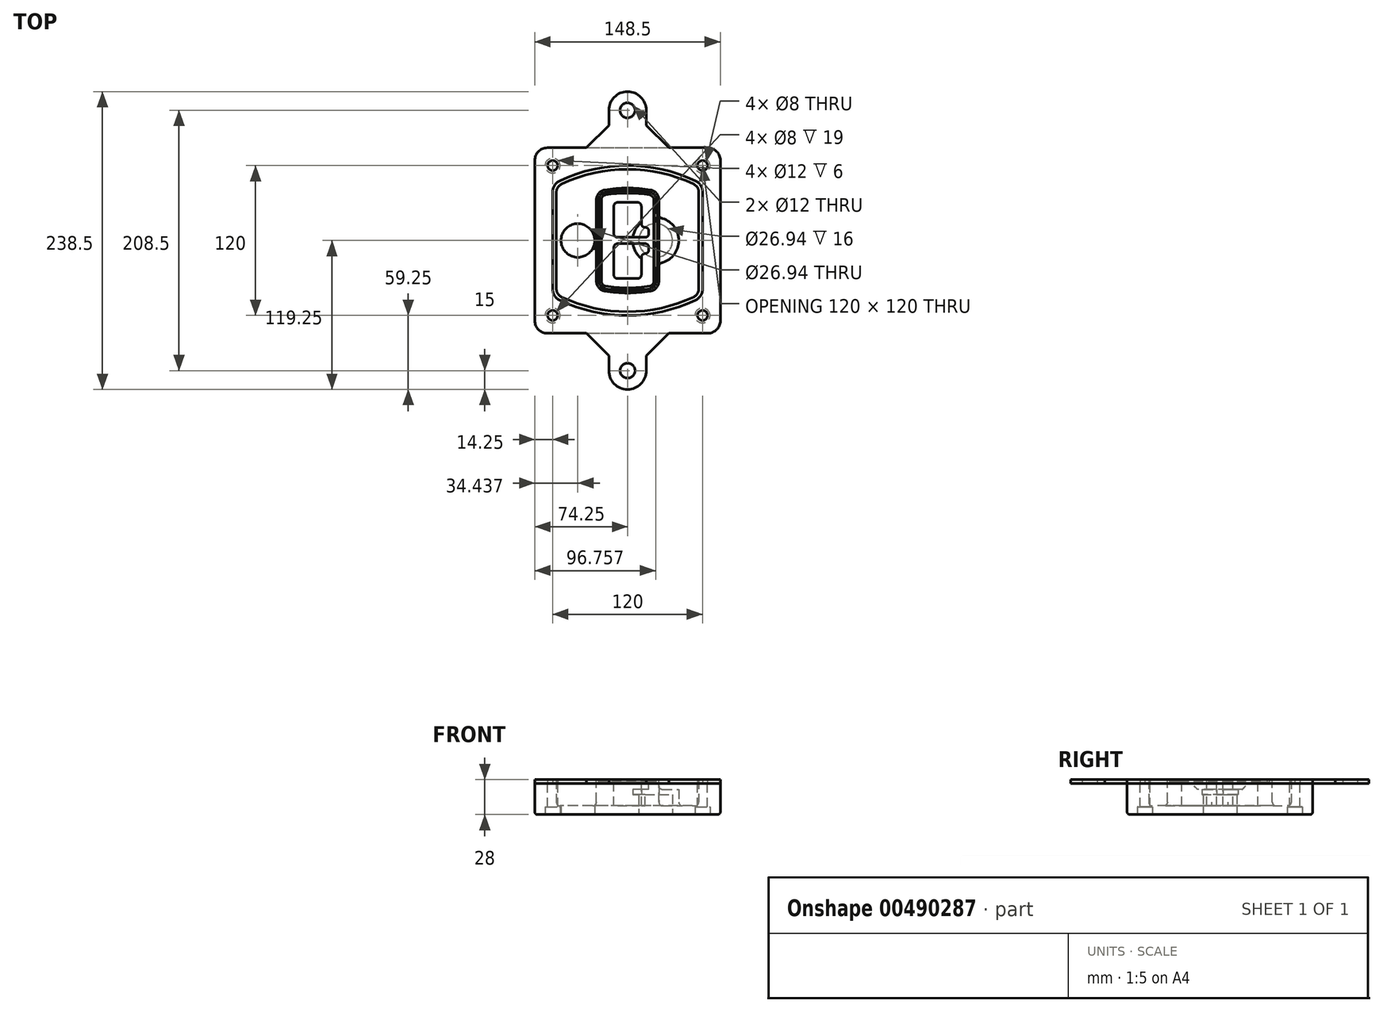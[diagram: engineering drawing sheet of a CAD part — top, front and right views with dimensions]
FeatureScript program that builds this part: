
annotation { "Feature Type Name" : "Feature", "Feature Type Description" : "" }
export const myFeature = defineFeature(function(context is Context, id is Id, definition is map)
    precondition{}
    {
        {
            var Q0;
            Q0=qCreatedBy(makeId("Top.planeOp"),FACE);
            var sketch = newSketch(context, id + "F0", { "sketchPlane" : qUnion([Q0])});
            skPoint(sketch, "E0.rect.middle", {"position": v(0, 0) * mm});
            skLineSegment(sketch, "E1.bottom", {"start": v(-64.25, -74.25) * mm, "end": v(64.25, -74.25) * mm});
            skLineSegment(sketch, "E1.top", {"start": v(-64.25, 74.25) * mm, "end": v(64.25, 74.25) * mm});
            skLineSegment(sketch, "E1.left", {"start": v(-74.25, -64.25) * mm, "end": v(-74.25, 64.25) * mm});
            skLineSegment(sketch, "E1.right", {"start": v(74.25, -64.25) * mm, "end": v(74.25, 64.25) * mm});
            skLineSegment(sketch, "E2", {"start": v(-74.25, 74.25) * mm, "end": v(74.25, -74.25) * mm, "construction": true});
            skLineSegment(sketch, "E3", {"start": v(74.25, 74.25) * mm, "end": v(-74.25, -74.25) * mm, "construction": true});
            skCircle(sketch, "E4", {"center": v(-60, 60) * mm, "radius": 4 * mm});
            skCircle(sketch, "E5", {"center": v(60, 60) * mm, "radius": 4 * mm});
            skCircle(sketch, "E6", {"center": v(60, -60) * mm, "radius": 4 * mm});
            skCircle(sketch, "E7", {"center": v(-60, -60) * mm, "radius": 4 * mm});
            skLineSegment(sketch, "E8", {"start": v(-60, 60) * mm, "end": v(60, 60) * mm, "construction": true});
            skLineSegment(sketch, "E9", {"start": v(60, 60) * mm, "end": v(60, -60) * mm, "construction": true});
            skLineSegment(sketch, "E10", {"start": v(60, -60) * mm, "end": v(-60, -60) * mm, "construction": true});
            skLineSegment(sketch, "E11", {"start": v(-60, -60) * mm, "end": v(-60, 60) * mm, "construction": true});
            skLineSegment(sketch, "E12", {"start": v(-60, 38.83) * mm, "end": v(-60, -38.83) * mm});
            skLineSegment(sketch, "E13", {"start": v(60, 38.83) * mm, "end": v(60, -38.83) * mm});
            skArc(sketch, "E14", {"start": v(54.26, 47.88) * mm, "mid": v(0, 60) * mm, "end": v(-54.26, 47.88) * mm});
            skArc(sketch, "E15", {"start": v(-54.26, -47.88) * mm, "mid": v(0, -60) * mm, "end": v(54.26, -47.88) * mm});
            skLineSegment(sketch, "E16", {"start": v(-60, 0) * mm, "end": v(60, 0) * mm, "construction": true});
            skPoint(sketch, "E17.visualSharp", {"position": v(-60, -45) * mm});
            skArc(sketch, "E17.filletArc", {"start": v(-60, -38.83) * mm, "mid": v(-58.44, -44.2) * mm, "end": v(-54.26, -47.88) * mm});
            skPoint(sketch, "E18.visualSharp", {"position": v(-60, 45) * mm});
            skArc(sketch, "E18.filletArc", {"start": v(-54.26, 47.88) * mm, "mid": v(-58.44, 44.2) * mm, "end": v(-60, 38.83) * mm});
            skPoint(sketch, "E19.visualSharp", {"position": v(60, 45) * mm});
            skArc(sketch, "E19.filletArc", {"start": v(60, 38.83) * mm, "mid": v(58.44, 44.2) * mm, "end": v(54.26, 47.88) * mm});
            skPoint(sketch, "E20.visualSharp", {"position": v(60, -45) * mm});
            skArc(sketch, "E20.filletArc", {"start": v(54.26, -47.88) * mm, "mid": v(58.44, -44.2) * mm, "end": v(60, -38.83) * mm});
            skPoint(sketch, "E21.visualSharp", {"position": v(-74.25, 74.25) * mm});
            skArc(sketch, "E21.filletArc", {"start": v(-64.25, 74.25) * mm, "mid": v(-71.32, 71.32) * mm, "end": v(-74.25, 64.25) * mm});
            skPoint(sketch, "E22.visualSharp", {"position": v(74.25, 74.25) * mm});
            skArc(sketch, "E22.filletArc", {"start": v(74.25, 64.25) * mm, "mid": v(71.32, 71.32) * mm, "end": v(64.25, 74.25) * mm});
            skPoint(sketch, "E23.visualSharp", {"position": v(74.25, -74.25) * mm});
            skArc(sketch, "E23.filletArc", {"start": v(64.25, -74.25) * mm, "mid": v(71.32, -71.32) * mm, "end": v(74.25, -64.25) * mm});
            skPoint(sketch, "E24.visualSharp", {"position": v(-74.25, -74.25) * mm});
            skArc(sketch, "E24.filletArc", {"start": v(-74.25, -64.25) * mm, "mid": v(-71.32, -71.32) * mm, "end": v(-64.25, -74.25) * mm});
            skArc(sketch, "E25.0", {"start": v(57, 38.83) * mm, "mid": v(55.9, 42.58) * mm, "end": v(52.98, 45.17) * mm});
            skLineSegment(sketch, "E25.1", {"start": v(57, 38.83) * mm, "end": v(57, -38.83) * mm});
            skArc(sketch, "E25.2", {"start": v(52.98, -45.17) * mm, "mid": v(55.9, -42.58) * mm, "end": v(57, -38.83) * mm});
            skArc(sketch, "E25.3", {"start": v(-52.98, -45.17) * mm, "mid": v(0, -57) * mm, "end": v(52.98, -45.17) * mm});
            skArc(sketch, "E25.4", {"start": v(-57, -38.83) * mm, "mid": v(-55.9, -42.58) * mm, "end": v(-52.98, -45.17) * mm});
            skArc(sketch, "E25.5", {"start": v(52.98, 45.17) * mm, "mid": v(0, 57) * mm, "end": v(-52.98, 45.17) * mm});
            skLineSegment(sketch, "E25.6", {"start": v(-57, 38.83) * mm, "end": v(-57, -38.83) * mm});
            skArc(sketch, "E25.7", {"start": v(-52.98, 45.17) * mm, "mid": v(-55.9, 42.58) * mm, "end": v(-57, 38.83) * mm});
            skArc(sketch, "E26.0", {"start": v(-55.96, 51.5) * mm, "mid": v(-61.82, 46.33) * mm, "end": v(-64, 38.83) * mm});
            skArc(sketch, "E26.1", {"start": v(55.96, 51.5) * mm, "mid": v(0, 64) * mm, "end": v(-55.96, 51.5) * mm});
            skArc(sketch, "E26.2", {"start": v(64, 38.83) * mm, "mid": v(61.82, 46.33) * mm, "end": v(55.96, 51.5) * mm});
            skLineSegment(sketch, "E26.3", {"start": v(64, 38.83) * mm, "end": v(64, -38.83) * mm});
            skArc(sketch, "E26.4", {"start": v(55.96, -51.5) * mm, "mid": v(61.82, -46.33) * mm, "end": v(64, -38.83) * mm});
            skLineSegment(sketch, "E26.5", {"start": v(-64, 38.83) * mm, "end": v(-64, -38.83) * mm});
            skArc(sketch, "E26.6", {"start": v(-55.96, -51.5) * mm, "mid": v(0, -64) * mm, "end": v(55.96, -51.5) * mm});
            skArc(sketch, "E26.7", {"start": v(-64, -38.83) * mm, "mid": v(-61.82, -46.33) * mm, "end": v(-55.96, -51.5) * mm});
            skSolve(sketch);
        }
        {
            var Q0;
            Q0=makeQuery(id+"F0.imprint","IMPRINT",FACE,{"disambiguationData":[TD([[makeQuery(id+"F0.imprint","IMPRINT",EDGE,{"derivedFrom":sQuery(id+"F0.wireOp",EDGE,"E1.bottom")}),1.0]])]});
            var Q1;
            Q1=makeQuery(id+"F0.imprint","IMPRINT",FACE,{"disambiguationData":[TD([[makeQuery(id+"F0.imprint","IMPRINT",EDGE,{"derivedFrom":sQuery(id+"F0.wireOp",EDGE,"E12")}),1.0]])]});
            var Q2;
            Q2=makeQuery(id+"F0.imprint","IMPRINT",FACE,{"disambiguationData":[TD([[makeQuery(id+"F0.imprint","IMPRINT",EDGE,{"derivedFrom":sQuery(id+"F0.wireOp",EDGE,"E25.0")}),1.0]])]});
            var Q3;
            Q3=makeQuery(id+"F0.imprint","IMPRINT",FACE,{"disambiguationData":[TD([[makeQuery(id+"F0.imprint","IMPRINT",EDGE,{"derivedFrom":sQuery(id+"F0.wireOp",EDGE,"E12")}),-1.0]])]});
            extrude(context, id + "F1", {"entities" : qUnion([Q0, Q1, Q2, Q3]), "oppositeDirection" : true, "depth" : 25 * mm});
        }
        {
            var Q0;
            Q0=makeQuery(id+"F0.imprint","IMPRINT",FACE,{"disambiguationData":[TD([[makeQuery(id+"F0.imprint","IMPRINT",EDGE,{"derivedFrom":sQuery(id+"F0.wireOp",EDGE,"E12")}),1.0]])]});
            extrude(context, id + "F2", {"entities" : qUnion([Q0]), "operationType" : NewBodyOperationType.ADD, "depth" : 3 * mm});
        }
        {
            var Q0;
            Q0=makeQuery(id+"F0.imprint","IMPRINT",FACE,{"disambiguationData":[TD([[makeQuery(id+"F0.imprint","IMPRINT",EDGE,{"derivedFrom":sQuery(id+"F0.wireOp",EDGE,"E25.0")}),1.0]])]});
            extrude(context, id + "F3", {"entities" : qUnion([Q0]), "operationType" : NewBodyOperationType.REMOVE, "oppositeDirection" : true, "depth" : 18 * mm});
        }
        {
            var Q0;
            Q0=makeQuery(id+"F2.opExtrude","CAP_FACE",FACE,{"disambiguationData":[OSD([sQuery(id+"F0.wireOp",EDGE,"E12"),sQuery(id+"F0.wireOp",EDGE,"E13"),sQuery(id+"F0.wireOp",EDGE,"E14"),sQuery(id+"F0.wireOp",EDGE,"E15"),sQuery(id+"F0.wireOp",EDGE,"E17.filletArc"),sQuery(id+"F0.wireOp",EDGE,"E18.filletArc"),sQuery(id+"F0.wireOp",EDGE,"E19.filletArc"),sQuery(id+"F0.wireOp",EDGE,"E20.filletArc"),sQuery(id+"F0.wireOp",EDGE,"E25.0"),sQuery(id+"F0.wireOp",EDGE,"E25.1"),sQuery(id+"F0.wireOp",EDGE,"E25.2"),sQuery(id+"F0.wireOp",EDGE,"E25.3"),sQuery(id+"F0.wireOp",EDGE,"E25.4"),sQuery(id+"F0.wireOp",EDGE,"E25.5"),sQuery(id+"F0.wireOp",EDGE,"E25.6"),sQuery(id+"F0.wireOp",EDGE,"E25.7")])],"isStart":false});
            var sketch = newSketch(context, id + "F4", { "sketchPlane" : qUnion([Q0])});
            skArc(sketch, "E27.0", {"start": v(-18.34, -40.45) * mm, "mid": v(0, -42) * mm, "end": v(18.34, -40.45) * mm});
            skArc(sketch, "E28.0", {"start": v(18.34, 40.45) * mm, "mid": v(0, 42) * mm, "end": v(-18.34, 40.45) * mm});
            skLineSegment(sketch, "E29", {"start": v(-25, 32.57) * mm, "end": v(-25, -32.57) * mm});
            skLineSegment(sketch, "E30", {"start": v(25, 32.57) * mm, "end": v(25, -32.57) * mm});
            skLineSegment(sketch, "E31", {"start": v(-25, 39.1) * mm, "end": v(25, 39.1) * mm, "construction": true});
            skLineSegment(sketch, "E32", {"start": v(-25, -39.1) * mm, "end": v(25, -39.1) * mm, "construction": true});
            skPoint(sketch, "E33.visualSharp", {"position": v(-25, 39.1) * mm});
            skArc(sketch, "E33.filletArc", {"start": v(-18.34, 40.45) * mm, "mid": v(-23.11, 37.73) * mm, "end": v(-25, 32.57) * mm});
            skPoint(sketch, "E34.visualSharp", {"position": v(25, 39.1) * mm});
            skArc(sketch, "E34.filletArc", {"start": v(25, 32.57) * mm, "mid": v(23.11, 37.73) * mm, "end": v(18.34, 40.45) * mm});
            skPoint(sketch, "E35.visualSharp", {"position": v(25, -39.1) * mm});
            skArc(sketch, "E35.filletArc", {"start": v(18.34, -40.45) * mm, "mid": v(23.11, -37.73) * mm, "end": v(25, -32.57) * mm});
            skPoint(sketch, "E36.visualSharp", {"position": v(-25, -39.1) * mm});
            skArc(sketch, "E36.filletArc", {"start": v(-25, -32.57) * mm, "mid": v(-23.11, -37.73) * mm, "end": v(-18.34, -40.45) * mm});
            skArc(sketch, "E37.0", {"start": v(52.98, 45.17) * mm, "mid": v(0, 57) * mm, "end": v(-52.98, 45.17) * mm});
            skArc(sketch, "E37.1", {"start": v(-52.98, 45.17) * mm, "mid": v(-55.9, 42.58) * mm, "end": v(-57, 38.83) * mm});
            skLineSegment(sketch, "E37.2", {"start": v(-57, 38.83) * mm, "end": v(-57, -38.83) * mm});
            skArc(sketch, "E37.3", {"start": v(-57, -38.83) * mm, "mid": v(-55.9, -42.58) * mm, "end": v(-52.98, -45.17) * mm});
            skArc(sketch, "E37.4", {"start": v(-52.98, -45.17) * mm, "mid": v(0, -57) * mm, "end": v(52.98, -45.17) * mm});
            skArc(sketch, "E37.5", {"start": v(52.98, -45.17) * mm, "mid": v(55.9, -42.58) * mm, "end": v(57, -38.83) * mm});
            skLineSegment(sketch, "E37.6", {"start": v(57, 38.83) * mm, "end": v(57, -38.83) * mm});
            skArc(sketch, "E37.7", {"start": v(57, 38.83) * mm, "mid": v(55.9, 42.58) * mm, "end": v(52.98, 45.17) * mm});
            skLineSegment(sketch, "E38.0", {"start": v(23, 32.57) * mm, "end": v(23, -32.57) * mm});
            skArc(sketch, "E38.1", {"start": v(18, -38.48) * mm, "mid": v(21.58, -36.44) * mm, "end": v(23, -32.57) * mm});
            skArc(sketch, "E38.2", {"start": v(-18, -38.48) * mm, "mid": v(0, -40) * mm, "end": v(18, -38.48) * mm});
            skArc(sketch, "E38.3", {"start": v(-23, -32.57) * mm, "mid": v(-21.58, -36.44) * mm, "end": v(-18, -38.48) * mm});
            skLineSegment(sketch, "E38.4", {"start": v(-23, 32.57) * mm, "end": v(-23, -32.57) * mm});
            skArc(sketch, "E38.5", {"start": v(23, 32.57) * mm, "mid": v(21.58, 36.44) * mm, "end": v(18, 38.48) * mm});
            skArc(sketch, "E38.6", {"start": v(-18, 38.48) * mm, "mid": v(-21.58, 36.44) * mm, "end": v(-23, 32.57) * mm});
            skArc(sketch, "E38.7", {"start": v(18, 38.48) * mm, "mid": v(0, 40) * mm, "end": v(-18, 38.48) * mm});
            skArc(sketch, "E39.0", {"start": v(21, 32.57) * mm, "mid": v(20.06, 35.15) * mm, "end": v(17.67, 36.5) * mm});
            skLineSegment(sketch, "E39.1", {"start": v(21, 32.57) * mm, "end": v(21, -32.57) * mm});
            skArc(sketch, "E39.2", {"start": v(17.67, -36.5) * mm, "mid": v(20.06, -35.15) * mm, "end": v(21, -32.57) * mm});
            skArc(sketch, "E39.3", {"start": v(-17.67, -36.5) * mm, "mid": v(0, -38) * mm, "end": v(17.67, -36.5) * mm});
            skArc(sketch, "E39.4", {"start": v(-21, -32.57) * mm, "mid": v(-20.06, -35.15) * mm, "end": v(-17.67, -36.5) * mm});
            skArc(sketch, "E39.5", {"start": v(17.67, 36.5) * mm, "mid": v(0, 38) * mm, "end": v(-17.67, 36.5) * mm});
            skLineSegment(sketch, "E39.6", {"start": v(-21, 32.57) * mm, "end": v(-21, -32.57) * mm});
            skArc(sketch, "E39.7", {"start": v(-17.67, 36.5) * mm, "mid": v(-20.06, 35.15) * mm, "end": v(-21, 32.57) * mm});
            skLineSegment(sketch, "E40", {"start": v(-25, 0) * mm, "end": v(25, 0) * mm, "construction": true});
            skLineSegment(sketch, "E41", {"start": v(-11, 5.5) * mm, "end": v(-11, 27.5) * mm});
            skLineSegment(sketch, "E42", {"start": v(-8, 30.5) * mm, "end": v(8, 30.5) * mm});
            skLineSegment(sketch, "E43", {"start": v(11, 27.5) * mm, "end": v(11, 13.5) * mm});
            skLineSegment(sketch, "E44", {"start": v(14, 10.5) * mm, "end": v(14, 10.5) * mm});
            skLineSegment(sketch, "E45", {"start": v(17, 7.5) * mm, "end": v(17, 5.5) * mm});
            skLineSegment(sketch, "E46", {"start": v(14, 2.5) * mm, "end": v(-8, 2.5) * mm});
            skPoint(sketch, "E47.visualSharp", {"position": v(-11, 30.5) * mm});
            skArc(sketch, "E47.filletArc", {"start": v(-8, 30.5) * mm, "mid": v(-10.12, 29.62) * mm, "end": v(-11, 27.5) * mm});
            skPoint(sketch, "E48.visualSharp", {"position": v(11, 30.5) * mm});
            skArc(sketch, "E48.filletArc", {"start": v(11, 27.5) * mm, "mid": v(10.12, 29.62) * mm, "end": v(8, 30.5) * mm});
            skPoint(sketch, "E49.visualSharp", {"position": v(11, 10.5) * mm});
            skArc(sketch, "E49.filletArc", {"start": v(11, 13.5) * mm, "mid": v(11.88, 11.38) * mm, "end": v(14, 10.5) * mm});
            skPoint(sketch, "E50.visualSharp", {"position": v(17, 10.5) * mm});
            skArc(sketch, "E50.filletArc", {"start": v(17, 7.5) * mm, "mid": v(16.12, 9.62) * mm, "end": v(14, 10.5) * mm});
            skPoint(sketch, "E51.visualSharp", {"position": v(17, 2.5) * mm});
            skArc(sketch, "E51.filletArc", {"start": v(14, 2.5) * mm, "mid": v(16.12, 3.38) * mm, "end": v(17, 5.5) * mm});
            skPoint(sketch, "E52.visualSharp", {"position": v(-11, 2.5) * mm});
            skArc(sketch, "E52.filletArc", {"start": v(-11, 5.5) * mm, "mid": v(-10.12, 3.38) * mm, "end": v(-8, 2.5) * mm});
            skLineSegment(sketch, "E53.0.MirrorCS", {"start": v(14, -2.5) * mm, "end": v(-8, -2.5) * mm});
            skArc(sketch, "E54.0.MirrorCS", {"start": v(-11, -5.5) * mm, "mid": v(-10.12, -3.38) * mm, "end": v(-8, -2.5) * mm});
            skLineSegment(sketch, "E55.0.MirrorCS", {"start": v(-11, -5.5) * mm, "end": v(-11, -27.5) * mm});
            skArc(sketch, "E56.0.MirrorCS", {"start": v(-8, -30.5) * mm, "mid": v(-10.12, -29.62) * mm, "end": v(-11, -27.5) * mm});
            skLineSegment(sketch, "E57.0.MirrorCS", {"start": v(-8, -30.5) * mm, "end": v(8, -30.5) * mm});
            skArc(sketch, "E58.0.MirrorCS", {"start": v(11, -27.5) * mm, "mid": v(10.12, -29.62) * mm, "end": v(8, -30.5) * mm});
            skLineSegment(sketch, "E59.0.MirrorCS", {"start": v(11, -27.5) * mm, "end": v(11, -13.5) * mm});
            skArc(sketch, "E60.0.MirrorCS", {"start": v(11, -13.5) * mm, "mid": v(11.88, -11.38) * mm, "end": v(14, -10.5) * mm});
            skArc(sketch, "E61.0.MirrorCS", {"start": v(17, -7.5) * mm, "mid": v(16.12, -9.62) * mm, "end": v(14, -10.5) * mm});
            skLineSegment(sketch, "E62.0.MirrorCS", {"start": v(17, -7.5) * mm, "end": v(17, -5.5) * mm});
            skArc(sketch, "E63.0.MirrorCS", {"start": v(14, -2.5) * mm, "mid": v(16.12, -3.38) * mm, "end": v(17, -5.5) * mm});
            skSolve(sketch);
        }
        {
            var Q0;
            Q0=makeQuery(id+"F4.imprint","IMPRINT",FACE,{"disambiguationData":[TD([[makeQuery(id+"F4.imprint","IMPRINT",EDGE,{"derivedFrom":sQuery(id+"F4.wireOp",EDGE,"E27.0")}),1.0]])]});
            var Q1;
            Q1=makeQuery(id+"F4.imprint","IMPRINT",FACE,{"disambiguationData":[TD([[makeQuery(id+"F4.imprint","IMPRINT",EDGE,{"derivedFrom":sQuery(id+"F4.wireOp",EDGE,"E38.0")}),-1.0]])]});
            var Q2;
            Q2=makeQuery(id+"F4.imprint","IMPRINT",FACE,{"disambiguationData":[TD([[makeQuery(id+"F4.imprint","IMPRINT",EDGE,{"derivedFrom":sQuery(id+"F4.wireOp",EDGE,"E39.0")}),1.0]])]});
            extrude(context, id + "F5", {"entities" : qUnion([Q0, Q1, Q2]), "operationType" : NewBodyOperationType.ADD, "endBound" : BoundingType.UP_TO_NEXT, "oppositeDirection" : true, "depth" : 25 * mm});
        }
        {
            var Q0;
            Q0=makeQuery(id+"F4.imprint","IMPRINT",FACE,{"disambiguationData":[TD([[makeQuery(id+"F4.imprint","IMPRINT",EDGE,{"derivedFrom":sQuery(id+"F4.wireOp",EDGE,"E38.0")}),-1.0]])]});
            extrude(context, id + "F6", {"entities" : qUnion([Q0]), "operationType" : NewBodyOperationType.REMOVE, "oppositeDirection" : true, "depth" : 2 * mm});
        }
        {
            var Q0;
            Q0=makeQuery(id+"F1.opExtrude","CAP_FACE",FACE,{"disambiguationData":[OSD([sQuery(id+"F0.wireOp",EDGE,"E1.bottom"),sQuery(id+"F0.wireOp",EDGE,"E1.top"),sQuery(id+"F0.wireOp",EDGE,"E1.left"),sQuery(id+"F0.wireOp",EDGE,"E1.right"),sQuery(id+"F0.wireOp",EDGE,"E4"),sQuery(id+"F0.wireOp",EDGE,"E5"),sQuery(id+"F0.wireOp",EDGE,"E6"),sQuery(id+"F0.wireOp",EDGE,"E7"),sQuery(id+"F0.wireOp",EDGE,"E21.filletArc"),sQuery(id+"F0.wireOp",EDGE,"E22.filletArc"),sQuery(id+"F0.wireOp",EDGE,"E23.filletArc"),sQuery(id+"F0.wireOp",EDGE,"E24.filletArc")])],"isStart":false});
            var sketch = newSketch(context, id + "F7", { "sketchPlane" : qUnion([Q0])});
            skCircle(sketch, "E64", {"center": v(22.5, 0) * mm, "radius": 13.47 * mm});
            skCircle(sketch, "E65", {"center": v(-39.81, 0) * mm, "radius": 13.47 * mm});
            skLineSegment(sketch, "E66", {"start": v(74.25, 0) * mm, "end": v(-74.25, 0) * mm});
            skCircle(sketch, "E67", {"center": v(22.5, 0) * mm, "radius": 18.47 * mm});
            skCircle(sketch, "E68", {"center": v(60, -60) * mm, "radius": 6 * mm});
            skCircle(sketch, "E69", {"center": v(-60, -60) * mm, "radius": 6 * mm});
            skCircle(sketch, "E70", {"center": v(-60, 60) * mm, "radius": 6 * mm});
            skCircle(sketch, "E71", {"center": v(60, 60) * mm, "radius": 6 * mm});
            skSolve(sketch);
        }
        {
            var Q0;
            {var subQ1=sQuery(id+"F7.wireOp",EDGE,"E66");var subQ4=sQuery(id+"F7.wireOp",EDGE,"E64");var subQ6=makeQuery(id+"F7.imprint","INTERSECT",VERTEX,{"disambiguationData":[OD(0.0)],"derivedFrom":[subQ4,subQ1]});Q0=makeQuery(id+"F7.imprint","IMPRINT",FACE,{"disambiguationData":[TD([[makeQuery(id+"F7.imprint","IMPRINT",EDGE,{"disambiguationData":[TD([[subQ6,-1.0]])],"derivedFrom":subQ4}),-1.0]])]});}
            var Q1;
            {var subQ0=sQuery(id+"F7.wireOp",EDGE,"E66");var subQ1=sQuery(id+"F7.wireOp",EDGE,"E64");var subQ3=makeQuery(id+"F7.imprint","INTERSECT",VERTEX,{"disambiguationData":[OD(0.0)],"derivedFrom":[subQ1,subQ0]});Q1=makeQuery(id+"F7.imprint","IMPRINT",FACE,{"disambiguationData":[TD([[makeQuery(id+"F7.imprint","IMPRINT",EDGE,{"disambiguationData":[TD([[subQ3,-1.0]])],"derivedFrom":subQ1}),1.0]])]});}
            var Q2;
            {var subQ0=sQuery(id+"F7.wireOp",EDGE,"E66");var subQ1=sQuery(id+"F7.wireOp",EDGE,"E64");var subQ3=makeQuery(id+"F7.imprint","INTERSECT",VERTEX,{"disambiguationData":[OD(0.0)],"derivedFrom":[subQ1,subQ0]});Q2=makeQuery(id+"F7.imprint","IMPRINT",FACE,{"disambiguationData":[TD([[makeQuery(id+"F7.imprint","IMPRINT",EDGE,{"disambiguationData":[TD([[subQ3,1.0]])],"derivedFrom":subQ1}),1.0]])]});}
            var Q3;
            {var subQ1=sQuery(id+"F7.wireOp",EDGE,"E66");var subQ4=sQuery(id+"F7.wireOp",EDGE,"E64");var subQ6=makeQuery(id+"F7.imprint","INTERSECT",VERTEX,{"disambiguationData":[OD(0.0)],"derivedFrom":[subQ4,subQ1]});Q3=makeQuery(id+"F7.imprint","IMPRINT",FACE,{"disambiguationData":[TD([[makeQuery(id+"F7.imprint","IMPRINT",EDGE,{"disambiguationData":[TD([[subQ6,1.0]])],"derivedFrom":subQ4}),-1.0]])]});}
            extrude(context, id + "F8", {"entities" : qUnion([Q0, Q1, Q2, Q3]), "operationType" : NewBodyOperationType.ADD, "oppositeDirection" : true, "depth" : 20 * mm});
        }
        {
            var Q0;
            {var subQ0=sQuery(id+"F7.wireOp",EDGE,"E66");var subQ1=sQuery(id+"F7.wireOp",EDGE,"E64");var subQ3=makeQuery(id+"F7.imprint","INTERSECT",VERTEX,{"disambiguationData":[OD(0.0)],"derivedFrom":[subQ1,subQ0]});Q0=makeQuery(id+"F7.imprint","IMPRINT",FACE,{"disambiguationData":[TD([[makeQuery(id+"F7.imprint","IMPRINT",EDGE,{"disambiguationData":[TD([[subQ3,-1.0]])],"derivedFrom":subQ1}),1.0]])]});}
            var Q1;
            {var subQ0=sQuery(id+"F7.wireOp",EDGE,"E66");var subQ1=sQuery(id+"F7.wireOp",EDGE,"E64");var subQ3=makeQuery(id+"F7.imprint","INTERSECT",VERTEX,{"disambiguationData":[OD(0.0)],"derivedFrom":[subQ1,subQ0]});Q1=makeQuery(id+"F7.imprint","IMPRINT",FACE,{"disambiguationData":[TD([[makeQuery(id+"F7.imprint","IMPRINT",EDGE,{"disambiguationData":[TD([[subQ3,1.0]])],"derivedFrom":subQ1}),1.0]])]});}
            extrude(context, id + "F9", {"entities" : qUnion([Q0, Q1]), "operationType" : NewBodyOperationType.REMOVE, "oppositeDirection" : true, "depth" : 16 * mm});
        }
        {
            var Q0;
            {var subQ0=sQuery(id+"F7.wireOp",EDGE,"E66");var subQ1=sQuery(id+"F7.wireOp",EDGE,"E65");var subQ3=makeQuery(id+"F7.imprint","INTERSECT",VERTEX,{"disambiguationData":[OD(0.0)],"derivedFrom":[subQ1,subQ0]});Q0=makeQuery(id+"F7.imprint","IMPRINT",FACE,{"disambiguationData":[TD([[makeQuery(id+"F7.imprint","IMPRINT",EDGE,{"disambiguationData":[TD([[subQ3,-1.0]])],"derivedFrom":subQ1}),1.0]])]});}
            var Q1;
            {var subQ0=sQuery(id+"F7.wireOp",EDGE,"E66");var subQ1=sQuery(id+"F7.wireOp",EDGE,"E65");var subQ3=makeQuery(id+"F7.imprint","INTERSECT",VERTEX,{"disambiguationData":[OD(0.0)],"derivedFrom":[subQ1,subQ0]});Q1=makeQuery(id+"F7.imprint","IMPRINT",FACE,{"disambiguationData":[TD([[makeQuery(id+"F7.imprint","IMPRINT",EDGE,{"disambiguationData":[TD([[subQ3,1.0]])],"derivedFrom":subQ1}),1.0]])]});}
            extrude(context, id + "F10", {"entities" : qUnion([Q0, Q1]), "operationType" : NewBodyOperationType.REMOVE, "oppositeDirection" : true, "depth" : 25 * mm});
        }
        {
            var Q0;
            Q0=makeQuery(id+"F7.imprint","IMPRINT",FACE,{"disambiguationData":[TD([[makeQuery(id+"F7.imprint","IMPRINT",EDGE,{"derivedFrom":sQuery(id+"F7.wireOp",EDGE,"E68")}),1.0]])]});
            var Q1;
            Q1=makeQuery(id+"F7.imprint","IMPRINT",FACE,{"disambiguationData":[TD([[makeQuery(id+"F7.imprint","IMPRINT",EDGE,{"derivedFrom":makeQuery(id+"F1.opExtrude","CAP_EDGE",EDGE,{"disambiguationData":[OSD([sQuery(id+"F0.wireOp",EDGE,"E5")])],"isStart":false})}),-1.0]])]});
            var Q2;
            Q2=makeQuery(id+"F7.imprint","IMPRINT",FACE,{"disambiguationData":[TD([[makeQuery(id+"F7.imprint","IMPRINT",EDGE,{"derivedFrom":sQuery(id+"F7.wireOp",EDGE,"E69")}),1.0]])]});
            var Q3;
            Q3=makeQuery(id+"F7.imprint","IMPRINT",FACE,{"disambiguationData":[TD([[makeQuery(id+"F7.imprint","IMPRINT",EDGE,{"derivedFrom":makeQuery(id+"F1.opExtrude","CAP_EDGE",EDGE,{"disambiguationData":[OSD([sQuery(id+"F0.wireOp",EDGE,"E4")])],"isStart":false})}),-1.0]])]});
            var Q4;
            Q4=makeQuery(id+"F7.imprint","IMPRINT",FACE,{"disambiguationData":[TD([[makeQuery(id+"F7.imprint","IMPRINT",EDGE,{"derivedFrom":sQuery(id+"F7.wireOp",EDGE,"E70")}),1.0]])]});
            var Q5;
            Q5=makeQuery(id+"F7.imprint","IMPRINT",FACE,{"disambiguationData":[TD([[makeQuery(id+"F7.imprint","IMPRINT",EDGE,{"derivedFrom":makeQuery(id+"F1.opExtrude","CAP_EDGE",EDGE,{"disambiguationData":[OSD([sQuery(id+"F0.wireOp",EDGE,"E7")])],"isStart":false})}),-1.0]])]});
            var Q6;
            Q6=makeQuery(id+"F7.imprint","IMPRINT",FACE,{"disambiguationData":[TD([[makeQuery(id+"F7.imprint","IMPRINT",EDGE,{"derivedFrom":sQuery(id+"F7.wireOp",EDGE,"E71")}),1.0]])]});
            var Q7;
            Q7=makeQuery(id+"F7.imprint","IMPRINT",FACE,{"disambiguationData":[TD([[makeQuery(id+"F7.imprint","IMPRINT",EDGE,{"derivedFrom":makeQuery(id+"F1.opExtrude","CAP_EDGE",EDGE,{"disambiguationData":[OSD([sQuery(id+"F0.wireOp",EDGE,"E6")])],"isStart":false})}),-1.0]])]});
            extrude(context, id + "F11", {"entities" : qUnion([Q0, Q1, Q2, Q3, Q4, Q5, Q6, Q7]), "operationType" : NewBodyOperationType.REMOVE, "oppositeDirection" : true, "depth" : 6 * mm});
        }
        {
            var Q0;
            Q0=makeQuery(id+"F9.boolean.opBoolean","COPY",FACE,{"derivedFrom":makeQuery(id+"F9.opExtrude","CAP_FACE",FACE,{"disambiguationData":[OSD([sQuery(id+"F7.wireOp",EDGE,"E64")])],"isStart":false})});
            var sketch = newSketch(context, id + "F12", { "sketchPlane" : qUnion([Q0])});
            skArc(sketch, "E72.0", {"start": v(11, 14.45) * mm, "mid": v(6.45, 9.13) * mm, "end": v(4.2, 2.5) * mm});
            skArc(sketch, "E72.1", {"start": v(4.2, -2.5) * mm, "mid": v(6.45, -9.13) * mm, "end": v(11, -14.45) * mm});
            skLineSegment(sketch, "E73", {"start": v(4.2, -2.5) * mm, "end": v(14, -2.5) * mm});
            skLineSegment(sketch, "E74.0", {"start": v(14, 2.5) * mm, "end": v(4.2, 2.5) * mm});
            skArc(sketch, "E74.1", {"start": v(14, 2.5) * mm, "mid": v(16.12, 3.38) * mm, "end": v(17, 5.5) * mm});
            skLineSegment(sketch, "E74.2", {"start": v(17, 7.5) * mm, "end": v(17, 5.5) * mm});
            skArc(sketch, "E74.3", {"start": v(17, 7.5) * mm, "mid": v(16.12, 9.62) * mm, "end": v(14, 10.5) * mm});
            skArc(sketch, "E74.4", {"start": v(11, 13.5) * mm, "mid": v(11.88, 11.38) * mm, "end": v(14, 10.5) * mm});
            skLineSegment(sketch, "E74.5", {"start": v(11, 14.45) * mm, "end": v(11, 13.5) * mm});
            skLineSegment(sketch, "E74.7", {"start": v(14, -2.5) * mm, "end": v(4.2, -2.5) * mm});
            skArc(sketch, "E74.8", {"start": v(14, -2.5) * mm, "mid": v(16.12, -3.38) * mm, "end": v(17, -5.5) * mm});
            skLineSegment(sketch, "E74.9", {"start": v(17, -7.5) * mm, "end": v(17, -5.5) * mm});
            skArc(sketch, "E74.10", {"start": v(17, -7.5) * mm, "mid": v(16.12, -9.62) * mm, "end": v(14, -10.5) * mm});
            skArc(sketch, "E74.11", {"start": v(11, -13.5) * mm, "mid": v(11.88, -11.38) * mm, "end": v(14, -10.5) * mm});
            skLineSegment(sketch, "E74.12", {"start": v(11, -14.45) * mm, "end": v(11, -13.5) * mm});
            skPoint(sketch, "E75.orphan", {"position": v(11, -27.5) * mm});
            skPoint(sketch, "E76.orphan", {"position": v(-8, -2.5) * mm});
            skPoint(sketch, "E77.orphan", {"position": v(-8, 2.5) * mm});
            skPoint(sketch, "E78.orphan", {"position": v(11, 27.5) * mm});
            skSolve(sketch);
        }
        {
            var Q0;
            {var subQ7=sQuery(id+"F12.wireOp",EDGE,"E72.0");var subQ14=sQuery(id+"F12.wireOp",EDGE,"E72.1");var subQ16=sQuery(id+"F12.wireOp",EDGE,"E74.1");var subQ18=sQuery(id+"F12.wireOp",EDGE,"E74.8");Q0=qUnion([makeQuery(id+"F12.imprint","IMPRINT",FACE,{"disambiguationData":[TD([[makeQuery(id+"F12.imprint","IMPRINT",EDGE,{"derivedFrom":subQ7}),1.0]])]}),makeQuery(id+"F12.imprint","IMPRINT",FACE,{"disambiguationData":[TD([[makeQuery(id+"F12.imprint","IMPRINT",EDGE,{"derivedFrom":subQ14}),1.0]])]}),makeQuery(id+"F12.imprint","IMPRINT",FACE,{"disambiguationData":[TD([[makeQuery(id+"F12.imprint","IMPRINT",EDGE,{"derivedFrom":subQ16}),1.0]])]}),makeQuery(id+"F12.imprint","IMPRINT",FACE,{"disambiguationData":[TD([[makeQuery(id+"F12.imprint","IMPRINT",EDGE,{"derivedFrom":subQ18}),-1.0]])]})]);}
            var Q1;
            Q1=makeQuery(id+"F5.boolean.opBoolean","SPLIT",FACE,{"disambiguationData":[TD([makeQuery(id+"F5.opExtrude","SWEPT_FACE",FACE,{"disambiguationData":[OSD([sQuery(id+"F4.wireOp",EDGE,"E41")])]})])],"derivedFrom":makeQuery(id+"F3.boolean.opBoolean","COPY",FACE,{"derivedFrom":makeQuery(id+"F3.opExtrude","CAP_FACE",FACE,{"disambiguationData":[OSD([sQuery(id+"F0.wireOp",EDGE,"E25.0"),sQuery(id+"F0.wireOp",EDGE,"E25.1"),sQuery(id+"F0.wireOp",EDGE,"E25.2"),sQuery(id+"F0.wireOp",EDGE,"E25.3"),sQuery(id+"F0.wireOp",EDGE,"E25.4"),sQuery(id+"F0.wireOp",EDGE,"E25.5"),sQuery(id+"F0.wireOp",EDGE,"E25.6"),sQuery(id+"F0.wireOp",EDGE,"E25.7")])],"isStart":false})})});
            extrude(context, id + "F13", {"entities" : qUnion([Q0]), "operationType" : NewBodyOperationType.REMOVE, "endBound" : BoundingType.UP_TO_SURFACE, "endBoundEntityFace" : qUnion([Q1]), "depth" : 25 * mm});
        }
        {
            var Q0;
            Q0=makeQuery(id+"F3.boolean.opBoolean","COPY",EDGE,{"derivedFrom":makeQuery(id+"F3.opExtrude","CAP_EDGE",EDGE,{"disambiguationData":[OSD([sQuery(id+"F0.wireOp",EDGE,"E25.6")])],"isStart":false})});
            var Q1;
            Q1=makeQuery(id+"F8.boolean.opBoolean","INTERSECT",EDGE,{"derivedFrom":[makeQuery(id+"F5.opExtrude","SWEPT_FACE",FACE,{"disambiguationData":[OSD([sQuery(id+"F4.wireOp",EDGE,"E30")])]}),makeQuery(id+"F8.opExtrude","CAP_FACE",FACE,{"disambiguationData":[OSD([sQuery(id+"F7.wireOp",EDGE,"E67")])],"isStart":false})]});
            var Q2;
            Q2=makeQuery(id+"F8.boolean.opBoolean","INTERSECT",EDGE,{"disambiguationData":[OD(1.0)],"derivedFrom":[makeQuery(id+"F5.opExtrude","SWEPT_FACE",FACE,{"disambiguationData":[OSD([sQuery(id+"F4.wireOp",EDGE,"E30")])]}),makeQuery(id+"F8.opExtrude","SWEPT_FACE",FACE,{"disambiguationData":[OSD([sQuery(id+"F7.wireOp",EDGE,"E67")])]})]});
            var Q3;
            {var subQ0=sQuery(id+"F4.wireOp",EDGE,"E30");Q3=makeQuery(id+"F8.boolean.opBoolean","SPLIT",EDGE,{"disambiguationData":[TD([makeQuery(id+"F5.opExtrude","SWEPT_FACE",FACE,{"disambiguationData":[OSD([sQuery(id+"F4.wireOp",EDGE,"E35.filletArc")])]})])],"derivedFrom":makeQuery(id+"F5.opExtrude","CAP_EDGE",EDGE,{"disambiguationData":[OSD([subQ0])],"isStart":false})});}
            var Q4;
            {var subQ0=sQuery(id+"F0.wireOp",EDGE,"E25.7");var subQ1=sQuery(id+"F0.wireOp",EDGE,"E25.1");var subQ2=sQuery(id+"F0.wireOp",EDGE,"E25.6");var subQ3=sQuery(id+"F0.wireOp",EDGE,"E25.5");var subQ4=sQuery(id+"F0.wireOp",EDGE,"E25.4");var subQ5=sQuery(id+"F0.wireOp",EDGE,"E25.0");var subQ6=sQuery(id+"F0.wireOp",EDGE,"E25.2");var subQ7=sQuery(id+"F0.wireOp",EDGE,"E25.3");Q4=makeQuery(id+"F8.boolean.opBoolean","INTERSECT",EDGE,{"derivedFrom":[makeQuery(id+"F5.boolean.opBoolean","SPLIT",FACE,{"disambiguationData":[TD([makeQuery(id+"F2.opExtrude","SWEPT_FACE",FACE,{"disambiguationData":[OSD([subQ5])]})])],"derivedFrom":makeQuery(id+"F3.boolean.opBoolean","COPY",FACE,{"derivedFrom":makeQuery(id+"F3.opExtrude","CAP_FACE",FACE,{"disambiguationData":[OSD([subQ5,subQ1,subQ6,subQ7,subQ4,subQ3,subQ2,subQ0])],"isStart":false})})}),makeQuery(id+"F8.opExtrude","SWEPT_FACE",FACE,{"disambiguationData":[OSD([sQuery(id+"F7.wireOp",EDGE,"E67")])]})]});}
            var Q5;
            Q5=makeQuery(id+"F8.boolean.opBoolean","INTERSECT",EDGE,{"disambiguationData":[OD(0.0)],"derivedFrom":[makeQuery(id+"F5.opExtrude","SWEPT_FACE",FACE,{"disambiguationData":[OSD([sQuery(id+"F4.wireOp",EDGE,"E30")])]}),makeQuery(id+"F8.opExtrude","SWEPT_FACE",FACE,{"disambiguationData":[OSD([sQuery(id+"F7.wireOp",EDGE,"E67")])]})]});
            fillet(context, id + "F14", {"entities" : qUnion([Q0, Q1, Q2, Q3, Q4, Q5]), "radius" : 3 * mm, "tangentPropagation" : true, "allowEdgeOverflow" : false});
        }
        {
            var Q0;
            Q0=makeQuery(id+"F1.opExtrude","CAP_EDGE",EDGE,{"disambiguationData":[OSD([sQuery(id+"F0.wireOp",EDGE,"E1.bottom")])],"isStart":false});
            fillet(context, id + "F15", {"entities" : qUnion([Q0]), "radius" : 2 * mm, "tangentPropagation" : true, "allowEdgeOverflow" : false});
        }
        {
            var Q0;
            {var subQ0=sQuery(id+"F0.wireOp",EDGE,"E21.filletArc");var subQ1=sQuery(id+"F0.wireOp",EDGE,"E7");var subQ2=sQuery(id+"F0.wireOp",EDGE,"E6");var subQ3=sQuery(id+"F0.wireOp",EDGE,"E5");var subQ4=sQuery(id+"F0.wireOp",EDGE,"E4");var subQ5=sQuery(id+"F0.wireOp",EDGE,"E22.filletArc");var subQ6=sQuery(id+"F0.wireOp",EDGE,"E1.bottom");var subQ7=sQuery(id+"F0.wireOp",EDGE,"E1.right");var subQ8=sQuery(id+"F0.wireOp",EDGE,"E1.top");var subQ9=sQuery(id+"F0.wireOp",EDGE,"E1.left");var subQ10=sQuery(id+"F0.wireOp",EDGE,"E23.filletArc");var subQ11=sQuery(id+"F0.wireOp",EDGE,"E24.filletArc");Q0=makeQuery(id+"F2.boolean.opBoolean","SPLIT",FACE,{"disambiguationData":[TD([makeQuery(id+"F1.opExtrude","SWEPT_FACE",FACE,{"disambiguationData":[OSD([subQ6])]})])],"derivedFrom":makeQuery(id+"F1.opExtrude","CAP_FACE",FACE,{"disambiguationData":[OSD([subQ6,subQ8,subQ9,subQ7,subQ4,subQ3,subQ2,subQ1,subQ0,subQ5,subQ10,subQ11])],"isStart":true})});}
            var sketch = newSketch(context, id + "F16", { "sketchPlane" : qUnion([Q0])});
            skLineSegment(sketch, "E79", {"start": v(0, 74.25) * mm, "end": v(0, 104.25) * mm, "construction": true});
            skArc(sketch, "E80", {"start": v(15, 104.25) * mm, "mid": v(0, 119.25) * mm, "end": v(-15, 104.25) * mm});
            skLineSegment(sketch, "E81", {"start": v(15, 104.25) * mm, "end": v(15, 92.25) * mm});
            skLineSegment(sketch, "E82", {"start": v(-15, 104.25) * mm, "end": v(-15, 92.25) * mm});
            skLineSegment(sketch, "E83", {"start": v(-15, 92.25) * mm, "end": v(-33, 74.25) * mm});
            skLineSegment(sketch, "E84", {"start": v(15, 92.25) * mm, "end": v(33, 74.25) * mm});
            skCircle(sketch, "E85", {"center": v(0, 104.25) * mm, "radius": 6 * mm});
            skLineSegment(sketch, "E86", {"start": v(-74.25, 0) * mm, "end": v(74.25, 0) * mm, "construction": true});
            skLineSegment(sketch, "E87.MirrorCS", {"start": v(-15, -92.25) * mm, "end": v(-33, -74.25) * mm});
            skLineSegment(sketch, "E88.MirrorCS", {"start": v(-15, -104.25) * mm, "end": v(-15, -92.25) * mm});
            skCircle(sketch, "E89.MirrorC", {"center": v(0, -104.25) * mm, "radius": 6 * mm});
            skLineSegment(sketch, "E90.MirrorCS", {"start": v(15, -104.25) * mm, "end": v(15, -92.25) * mm});
            skLineSegment(sketch, "E91.MirrorCS", {"start": v(0, -74.25) * mm, "end": v(0, -104.25) * mm, "construction": true});
            skLineSegment(sketch, "E92.MirrorCS", {"start": v(15, -92.25) * mm, "end": v(33, -74.25) * mm});
            skArc(sketch, "E93.MirrorCS", {"start": v(15, -104.25) * mm, "mid": v(0, -119.25) * mm, "end": v(-15, -104.25) * mm});
            skSolve(sketch);
        }
        {
            var Q0;
            Q0=makeQuery(id+"F16.imprint","IMPRINT",FACE,{"disambiguationData":[TD([[makeQuery(id+"F16.imprint","IMPRINT",EDGE,{"derivedFrom":sQuery(id+"F16.wireOp",EDGE,"E80")}),1.0]])]});
            var Q1;
            Q1=makeQuery(id+"F16.imprint","IMPRINT",FACE,{"disambiguationData":[TD([[makeQuery(id+"F16.imprint","IMPRINT",EDGE,{"derivedFrom":makeQuery(id+"F1.opExtrude","CAP_EDGE",EDGE,{"disambiguationData":[OSD([sQuery(id+"F0.wireOp",EDGE,"E1.left")])],"isStart":true})}),-1.0]])]});
            var Q2;
            {var subQ0=sQuery(id+"F16.wireOp",EDGE,"E87.MirrorCS");Q2=makeQuery(id+"F16.imprint","IMPRINT",FACE,{"disambiguationData":[TD([[makeQuery(id+"F16.imprint","IMPRINT",EDGE,{"derivedFrom":subQ0}),-1.0]])]});}
            var Q3;
            Q3=makeQuery(id+"F2.opExtrude","CAP_FACE",FACE,{"disambiguationData":[OSD([sQuery(id+"F0.wireOp",EDGE,"E12"),sQuery(id+"F0.wireOp",EDGE,"E13"),sQuery(id+"F0.wireOp",EDGE,"E14"),sQuery(id+"F0.wireOp",EDGE,"E15"),sQuery(id+"F0.wireOp",EDGE,"E17.filletArc"),sQuery(id+"F0.wireOp",EDGE,"E18.filletArc"),sQuery(id+"F0.wireOp",EDGE,"E19.filletArc"),sQuery(id+"F0.wireOp",EDGE,"E20.filletArc"),sQuery(id+"F0.wireOp",EDGE,"E25.0"),sQuery(id+"F0.wireOp",EDGE,"E25.1"),sQuery(id+"F0.wireOp",EDGE,"E25.2"),sQuery(id+"F0.wireOp",EDGE,"E25.3"),sQuery(id+"F0.wireOp",EDGE,"E25.4"),sQuery(id+"F0.wireOp",EDGE,"E25.5"),sQuery(id+"F0.wireOp",EDGE,"E25.6"),sQuery(id+"F0.wireOp",EDGE,"E25.7")])],"isStart":false});
            extrude(context, id + "F17", {"entities" : qUnion([Q0, Q1, Q2]), "endBound" : BoundingType.UP_TO_SURFACE, "endBoundEntityFace" : qUnion([Q3]), "depth" : 25 * mm});
        }
    });
